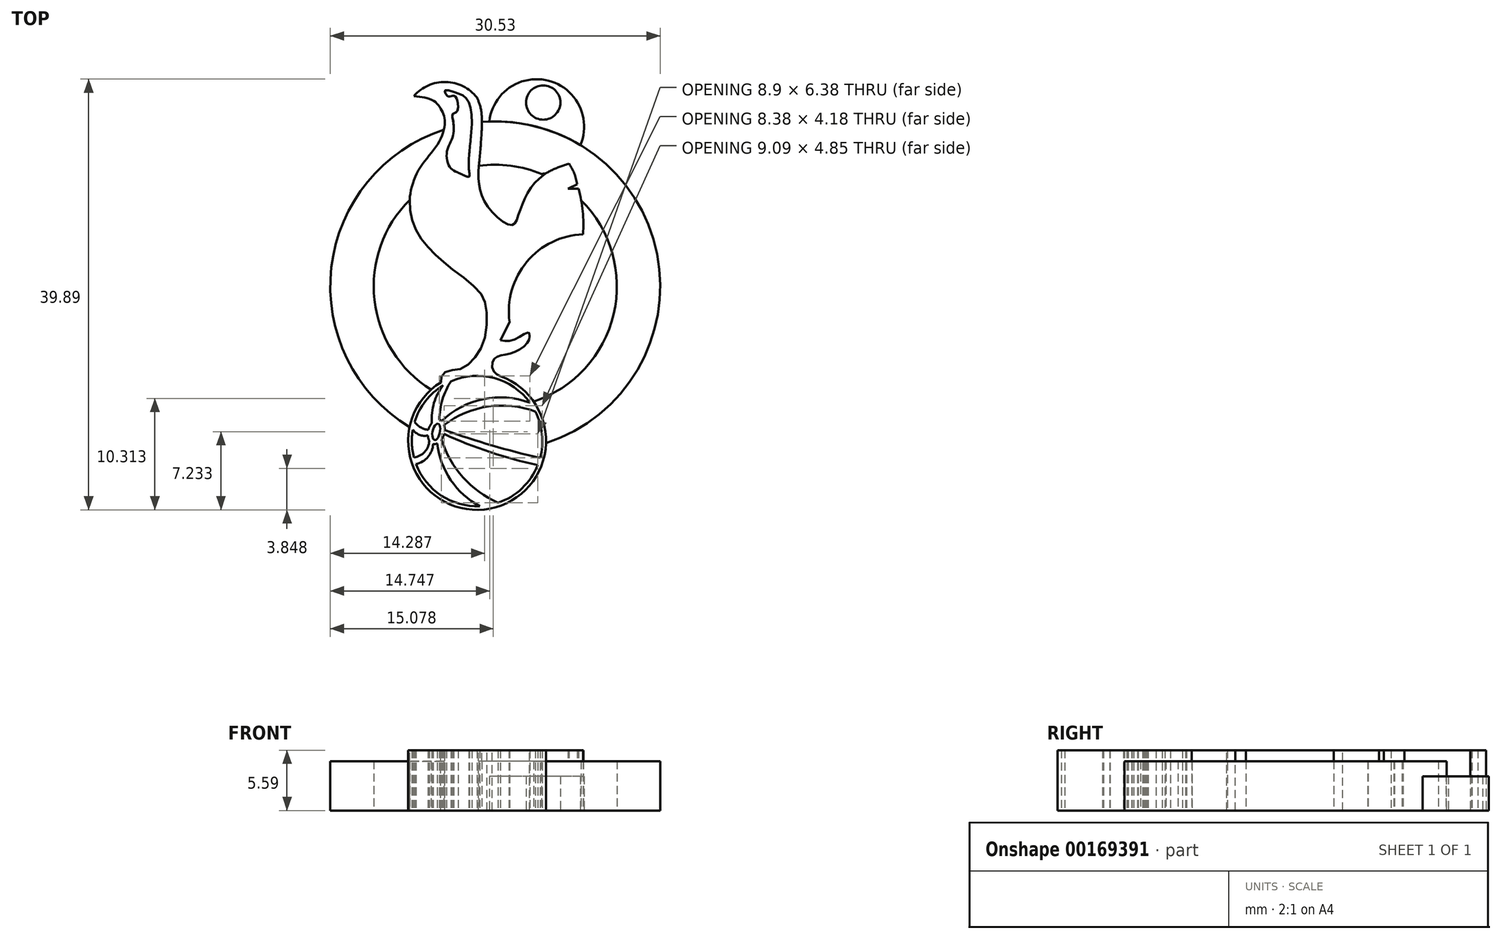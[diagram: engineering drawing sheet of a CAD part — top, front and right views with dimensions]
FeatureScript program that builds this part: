
annotation { "Feature Type Name" : "Feature", "Feature Type Description" : "" }
export const myFeature = defineFeature(function(context is Context, id is Id, definition is map)
    precondition{}
    {
        {
            var Q0;
            Q0=qCreatedBy(makeId("Top.planeOp"),FACE);
            var sketch = newSketch(context, id + "F0", { "sketchPlane" : qUnion([Q0])});
            skArc(sketch, "E0", {"start": v(9.47, 28.93) * mm, "mid": v(6.59, 30.38) * mm, "end": v(3.64, 29.06) * mm});
            skFitSpline(sketch, "E1", {"points": [v(9.47, 28.93) * mm, v(9.88, 27.6) * mm, v(9.73, 23.52) * mm, v(9.68, 20.77) * mm, v(10.71, 18.5) * mm, v(12.7, 17.13) * mm, v(13.25, 17.88) * mm, v(14.13, 20.04) * mm, v(15.77, 21.86) * mm, v(17.98, 22.83) * mm], "startDerivative": vector(5.88, -12.64) * mm, "endDerivative": vector(20.31, 7) * mm});
            skArc(sketch, "E2", {"start": v(18.74, 20.91) * mm, "mid": v(18.47, 21.91) * mm, "end": v(17.98, 22.83) * mm});
            skLineSegment(sketch, "E3", {"start": v(18.74, 20.91) * mm, "end": v(17.89, 20.48) * mm});
            skLineSegment(sketch, "E4", {"start": v(17.89, 20.48) * mm, "end": v(18.89, 20.48) * mm});
            skArc(sketch, "E5", {"start": v(19.3, 16.28) * mm, "mid": v(19.25, 18.4) * mm, "end": v(18.89, 20.48) * mm});
            skArc(sketch, "E6", {"start": v(19.3, 16.28) * mm, "mid": v(14.09, 13.72) * mm, "end": v(12.49, 8.15) * mm});
            skLineSegment(sketch, "E7", {"start": v(12.49, 8.15) * mm, "end": v(11.64, 6.46) * mm});
            skFitSpline(sketch, "E8", {"points": [v(11.64, 6.46) * mm, v(12.74, 6.46) * mm, v(14.02, 7.12) * mm, v(14.29, 7.14) * mm, v(14.34, 6.71) * mm, v(13.95, 6) * mm, v(12.68, 5.27) * mm, v(11.64, 5.04) * mm, v(11.01, 4.65) * mm, v(10.98, 3.67) * mm, v(11.64, 3.13) * mm], "startDerivative": vector(9.48, -1.66) * mm, "endDerivative": vector(8.07, -4.1) * mm});
            skArc(sketch, "E9", {"start": v(6.14, 2.56) * mm, "mid": v(10.14, -9.22) * mm, "end": v(11.64, 3.13) * mm});
            skFitSpline(sketch, "E10", {"points": [v(6.14, 2.56) * mm, v(6.19, 3.11) * mm, v(6.77, 3.6) * mm, v(7.92, 3.79) * mm, v(9.2, 4.75) * mm, v(10.22, 6.83) * mm, v(10.3, 9.6) * mm, v(9.6, 11.07) * mm, v(7.2, 13.04) * mm, v(5.43, 14.6) * mm, v(4.06, 16.23) * mm, v(3.36, 18.04) * mm, v(3.32, 20.13) * mm, v(4.3, 22.6) * mm, v(5.92, 24.74) * mm, v(6.5, 26.63) * mm, v(6.21, 27.75) * mm, v(5.4, 28.67) * mm, v(3.64, 29.06) * mm], "startDerivative": vector(-1.68, 18.33) * mm, "endDerivative": vector(-35.26, 3.54) * mm});
            skFitSpline(sketch, "E11", {"points": [v(6.5, 29.56) * mm, v(7.53, 29.4) * mm, v(8.48, 28.87) * mm, v(9, 26.93) * mm, v(8.71, 22.48) * mm, v(8.74, 21.6) * mm, v(7.93, 21.9) * mm, v(7, 22.44) * mm, v(6.7, 23.9) * mm, v(7.17, 25.14) * mm, v(7.29, 26.63) * mm, v(7.22, 27.4) * mm, v(7.57, 27.6) * mm, v(7.72, 28.35) * mm, v(7.43, 29.06) * mm, v(7.1, 29.06) * mm, v(6.77, 29.06) * mm, v(6.5, 29.56) * mm]});
            skCircle(sketch, "E12", {"center": v(9.48, -2.87) * mm, "radius": 6.04 * mm});
            skArc(sketch, "E13", {"start": v(14.34, 0.66) * mm, "mid": v(14.36, 0.66) * mm, "end": v(14.38, 0.67) * mm});
            skArc(sketch, "E14.trimOffspring", {"start": v(14.72, 0.78) * mm, "mid": v(22.12, 8.87) * mm, "end": v(19.12, 19.42) * mm});
            skEllipse(sketch, "E15", {"center": v(5.7, -2.02) * mm, "majorRadius": 1.16 * mm, "minorRadius": 0.75 * mm, "majorAxis": v(0.25, 0.97)});
            skArc(sketch, "E16", {"start": v(6.34, 2.28) * mm, "mid": v(5.5, 0.64) * mm, "end": v(5.3, -1.2) * mm});
            skArc(sketch, "E17", {"start": v(7.06, 2.66) * mm, "mid": v(6.28, 0.95) * mm, "end": v(6, -0.9) * mm});
            skArc(sketch, "E18", {"start": v(3.7, -1.1) * mm, "mid": v(4.26, -1.61) * mm, "end": v(4.98, -1.83) * mm});
            skArc(sketch, "E19", {"start": v(3.54, -1.82) * mm, "mid": v(4.15, -2.3) * mm, "end": v(4.93, -2.37) * mm});
            skArc(sketch, "E20", {"start": v(5.8, -3.1) * mm, "mid": v(7.05, -6.5) * mm, "end": v(9.74, -8.9) * mm});
            skArc(sketch, "E21", {"start": v(6.2, -2.74) * mm, "mid": v(8.18, -6.23) * mm, "end": v(11.42, -8.6) * mm});
            skArc(sketch, "E22", {"start": v(6.43, -2.21) * mm, "mid": v(10.68, -3.9) * mm, "end": v(15.1, -5.1) * mm});
            skArc(sketch, "E23", {"start": v(6.49, -1.86) * mm, "mid": v(10.86, -3.28) * mm, "end": v(15.32, -4.44) * mm});
            skArc(sketch, "E24", {"start": v(14.38, 0.67) * mm, "mid": v(10.05, 1) * mm, "end": v(6.22, -1.02) * mm});
            skArc(sketch, "E25", {"start": v(14.87, -0.15) * mm, "mid": v(10.5, 0.32) * mm, "end": v(6.43, -1.38) * mm});
            skArc(sketch, "E26", {"start": v(3.84, -5.01) * mm, "mid": v(4.94, -4.35) * mm, "end": v(5.41, -3.14) * mm});
            skArc(sketch, "E27", {"start": v(3.64, -4.4) * mm, "mid": v(4.64, -3.88) * mm, "end": v(5.06, -2.85) * mm});
            skArc(sketch, "E28", {"start": v(4.74, -2.4) * mm, "mid": v(4.84, -2.44) * mm, "end": v(4.94, -2.48) * mm});
            skArc(sketch, "E29.trimOffspring", {"start": v(6.04, -2.92) * mm, "mid": v(6.16, -2.97) * mm, "end": v(6.28, -3) * mm});
            skArc(sketch, "E30.trimOffspring", {"start": v(15.86, -3.07) * mm, "mid": v(26.14, 14.44) * mm, "end": v(9.93, 26.67) * mm});
            skArc(sketch, "E31.trimOffspring", {"start": v(3.25, 19.46) * mm, "mid": v(-0.02, 10.2) * mm, "end": v(5.24, 1.89) * mm});
            skArc(sketch, "E32.trimOffspring", {"start": v(8.72, 22.44) * mm, "mid": v(8.09, 22.28) * mm, "end": v(7.47, 22.09) * mm});
            skArc(sketch, "E33.trimOffspring", {"start": v(6.42, 25.96) * mm, "mid": v(-4, 13.2) * mm, "end": v(3.24, -1.59) * mm});
            skArc(sketch, "E34.trimOffspring", {"start": v(9, 26.57) * mm, "mid": v(8.16, 26.42) * mm, "end": v(7.33, 26.23) * mm});
            skArc(sketch, "E35.trimOffspring", {"start": v(15.66, 21.78) * mm, "mid": v(12.71, 22.6) * mm, "end": v(9.65, 22.6) * mm});
            skEllipse(sketch, "E36", {"center": v(5.7, -2.02) * mm, "majorRadius": 0.77 * mm, "minorRadius": 0.34 * mm, "majorAxis": v(0.2, 0.98)});
            skArc(sketch, "E37", {"start": v(15.46, 21.86) * mm, "mid": v(15.67, 21.89) * mm, "end": v(15.87, 21.92) * mm});
            skCircle(sketch, "E38", {"center": v(15.6, 28.47) * mm, "radius": 1.59 * mm});
            skArc(sketch, "E39.trimOffspring", {"start": v(19.05, 24.53) * mm, "mid": v(16.1, 30.5) * mm, "end": v(10.62, 26.71) * mm});
            skSolve(sketch);
        }
        {
            var Q0;
            {var subQ13=sQuery(id+"F0.wireOp",EDGE,"E0");Q0=makeQuery(id+"F0.imprint","IMPRINT",FACE,{"disambiguationData":[TD([[makeQuery(id+"F0.imprint","IMPRINT",EDGE,{"derivedFrom":subQ13}),1.0]])]});}
            var Q1;
            {var subQ0=sQuery(id+"F0.wireOp",EDGE,"E24");Q1=makeQuery(id+"F0.imprint","IMPRINT",FACE,{"disambiguationData":[TD([[makeQuery(id+"F0.imprint","IMPRINT",EDGE,{"derivedFrom":subQ0}),1.0]])]});}
            var Q2;
            {var subQ0=sQuery(id+"F0.wireOp",EDGE,"E16");Q2=makeQuery(id+"F0.imprint","IMPRINT",FACE,{"disambiguationData":[TD([[makeQuery(id+"F0.imprint","IMPRINT",EDGE,{"derivedFrom":subQ0}),1.0]])]});}
            var Q3;
            {var subQ4=sQuery(id+"F0.wireOp",EDGE,"E18");Q3=makeQuery(id+"F0.imprint","IMPRINT",FACE,{"disambiguationData":[TD([[makeQuery(id+"F0.imprint","IMPRINT",EDGE,{"derivedFrom":subQ4}),-1.0]])]});}
            var Q4;
            {var subQ0=sQuery(id+"F0.wireOp",EDGE,"E26");Q4=makeQuery(id+"F0.imprint","IMPRINT",FACE,{"disambiguationData":[TD([[makeQuery(id+"F0.imprint","IMPRINT",EDGE,{"derivedFrom":subQ0}),1.0]])]});}
            var Q5;
            {var subQ4=sQuery(id+"F0.wireOp",EDGE,"E20");Q5=makeQuery(id+"F0.imprint","IMPRINT",FACE,{"disambiguationData":[TD([[makeQuery(id+"F0.imprint","IMPRINT",EDGE,{"derivedFrom":subQ4}),1.0]])]});}
            var Q6;
            {var subQ0=sQuery(id+"F0.wireOp",EDGE,"E22");Q6=makeQuery(id+"F0.imprint","IMPRINT",FACE,{"disambiguationData":[TD([[makeQuery(id+"F0.imprint","IMPRINT",EDGE,{"derivedFrom":subQ0}),1.0]])]});}
            var Q7;
            {var subQ3=sQuery(id+"F0.wireOp",EDGE,"E29.trimOffspring");Q7=makeQuery(id+"F0.imprint","IMPRINT",FACE,{"disambiguationData":[TD([[makeQuery(id+"F0.imprint","IMPRINT",EDGE,{"derivedFrom":subQ3}),1.0]])]});}
            var Q8;
            Q8=makeQuery(id+"F0.imprint","IMPRINT",FACE,{"disambiguationData":[TD([[makeQuery(id+"F0.imprint","IMPRINT",EDGE,{"derivedFrom":sQuery(id+"F0.wireOp",EDGE,"E36")}),-1.0]])]});
            extrude(context, id + "F1", {"entities" : qUnion([Q0, Q1, Q2, Q3, Q4, Q5, Q6, Q7, Q8]), "depth" : 5.6 * mm});
        }
        {
            var Q0;
            {var subQ1=sQuery(id+"F0.wireOp",EDGE,"E2");Q0=makeQuery(id+"F0.imprint","IMPRINT",FACE,{"disambiguationData":[TD([[makeQuery(id+"F0.imprint","IMPRINT",EDGE,{"derivedFrom":subQ1}),-1.0]])]});}
            var Q1;
            {var subQ0=sQuery(id+"F0.wireOp",EDGE,"E31.trimOffspring");Q1=makeQuery(id+"F0.imprint","IMPRINT",FACE,{"disambiguationData":[TD([[makeQuery(id+"F0.imprint","IMPRINT",EDGE,{"derivedFrom":subQ0}),-1.0]])]});}
            extrude(context, id + "F2", {"entities" : qUnion([Q0, Q1]), "operationType" : NewBodyOperationType.ADD, "depth" : 4.57 * mm});
        }
        {
            var Q0;
            Q0=makeQuery(id+"F0.imprint","IMPRINT",FACE,{"disambiguationData":[TD([[makeQuery(id+"F0.imprint","IMPRINT",EDGE,{"derivedFrom":sQuery(id+"F0.wireOp",EDGE,"E38")}),-1.0]])]});
            extrude(context, id + "F3", {"entities" : qUnion([Q0]), "operationType" : NewBodyOperationType.ADD, "depth" : 3.17 * mm});
        }
    });
